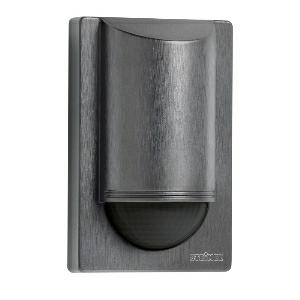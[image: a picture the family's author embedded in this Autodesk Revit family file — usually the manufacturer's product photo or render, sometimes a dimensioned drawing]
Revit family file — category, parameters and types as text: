
# Revit family: is_2180-2_057664
name_source: partatom
category: Elektroinstallationen
revit_build: Autodesk Revit 2016 (Build: 20190508_0715(x64)
units: mm (PartAtom-declared; Revit-internal decimal feet)

## family parameters
Basisbauteil = Fläche
Beim Laden mit Abzugskörper schneiden = Nein
Bemaßung runder Anschluss = Durchmesser verwenden
Beschriftungsausrichtung beibehalten = Nein
Gemeinsam genutzt = Nein
Raumberechnungspunkt = Nein
Teiletyp = Normal

## types (1)
- IS 2180-2
    Apparent Load = 0 VA
    Beschreibung = Type: Motion detectors; Dimensions (L x W x H): 55 x 78 x 120 mm; Mains power supply: 230 V / 50 Hz; Power consumption: 0,5 W; Sensor Technology: passive infrared; Application, place: Indoors, Outdoors; Application, room: outdoors, front door, all round the building, terrace / balcony, courtyard & driveway; Installation site: wall, corner; Installation: Surface wiring; Switching zones: 508 switching zones; Electronic scalability: No; Mechanical scalability: No; Mounting height: 1,8 – 4 m; Optimum mounting height: 2 m; Detection angle: 180 °; Angle of aperture: 90 °; Sneak-by guard: Yes; Capability of masking out individual segments: Yes; Reach, radial: r = 2 m (6 m²) / r = 4 m (25 m²); Reach, tangential: r = 5 m (39 m²) / r = 12 m (226 m²); Twilight setting TEACH: No; Twilight setting: 2 – 2000 lx; Time setting: 5 sec – 15 min; Switching output 1, resistive: 1000 W; Switching output 1, number of LEDs / fluorescent lamps: 6 pcs.; Switching output 1, floating: No; Constant-lighting control: No; Basic light level function: No; Settings via: Potentiometers; With remote control: No; Interconnection: Yes; IP-rating: IP54; Material: Plastic; Ambient temperature: -20 – 50 °C; Colour: Anthracite; Manufacturer's Warranty: 5 years; Version: Anthracite; PU1, EAN: 4007841057664
    Height = 120 mm  [stored 0.393701 ft]
    Hersteller = Steinel
    Length = 55 mm
    Maximum range = 14.375 m
    ModVariant = Nein
    Modell = 057664
    Mounting Type = Surface mounted
    Number of Poles = 1
    OnlyDefault = Ja
    Power Factor = 1
    Product Name = IS 2180-2
    Product group = Sensor-switched indoor light
    ProductGroupID = 30
    Protection Class = Protection class
    Protection Degree = IP 54
    RlxData = <blob elided: 170857 chars, md5=6fda3605>
    Sensor characteristics = Semi circular 145°-300°
    Sensor type = Passive (infrared)
    SensorDataFile = <blob elided: 4407 chars, md5=e7ee70d0>
    Type of entry = Motion
    Typenbild = produkt1_057664.jpg
    Typenkommentare = Product without accessories
    URL = http://relux.com
    VarID = ---
    Voltage = 0 V
    Vorgabe-Ansicht = 1800 mm
    Weight = 0.00 kg
    Width = 78 mm  [stored 0.255906 ft]

note: [stored X ft] marks values corroborated as IEEE doubles in the binary element streams (Revit-internal decimal feet)

## geometry (parser evidence)
native form markers: Sweep x17
no freeform markers — native parametric forms only
